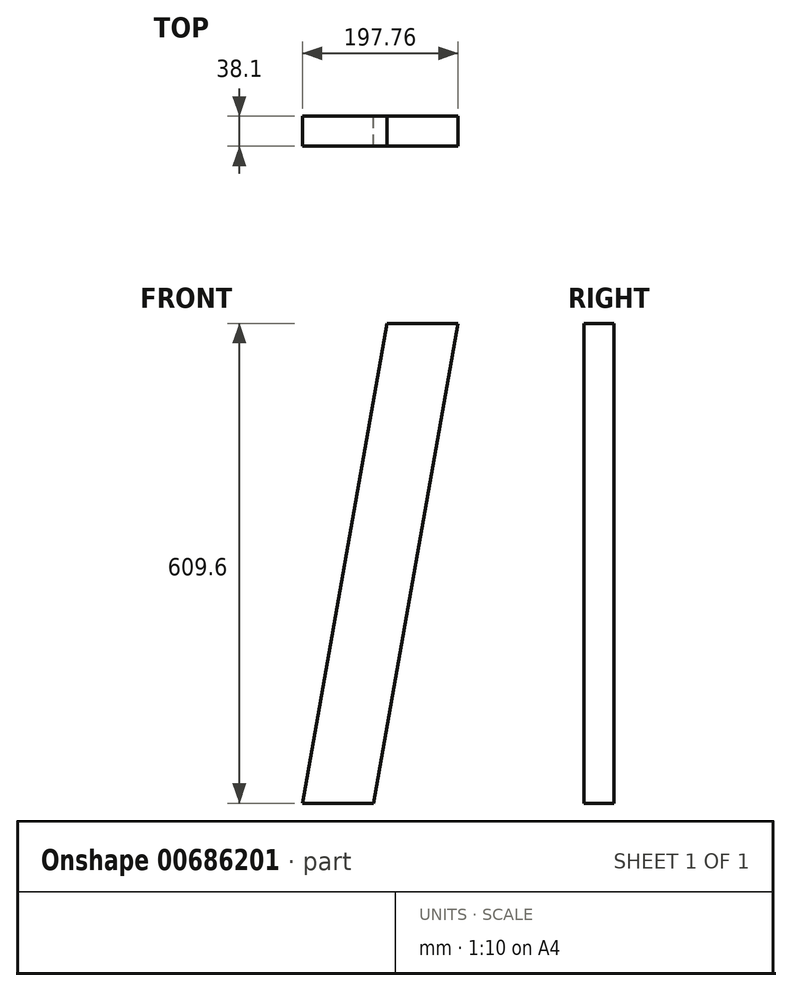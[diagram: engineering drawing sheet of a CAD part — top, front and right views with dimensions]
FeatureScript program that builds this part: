
annotation { "Feature Type Name" : "Feature", "Feature Type Description" : "" }
export const myFeature = defineFeature(function(context is Context, id is Id, definition is map)
    precondition{}
    {
        {
            var Q0;
            Q0=qCreatedBy(makeId("Front.planeOp"),FACE);
            var sketch = newSketch(context, id + "F0", { "sketchPlane" : qUnion([Q0])});
            skLineSegment(sketch, "E0", {"start": v(0, 0) * mm, "end": v(-107.49, -609.6) * mm});
            skLineSegment(sketch, "E1", {"start": v(-107.49, -609.6) * mm, "end": v(-17.22, -609.6) * mm});
            skLineSegment(sketch, "E2", {"start": v(-17.22, -609.6) * mm, "end": v(90.27, 0) * mm});
            skLineSegment(sketch, "E3", {"start": v(90.27, 0) * mm, "end": v(0, 0) * mm});
            skLineSegment(sketch, "E4", {"start": v(0, 0) * mm, "end": v(0, -569.46) * mm, "construction": true});
            skSolve(sketch);
        }
        {
            var Q0;
            Q0 = qSketchRegion(id + "F0", true);
            extrude(context, id + "F1", {"entities" : qUnion([Q0]), "depth" : 38.1 * mm, "offsetDistance" : 25.4 * mm});
        }
    });
